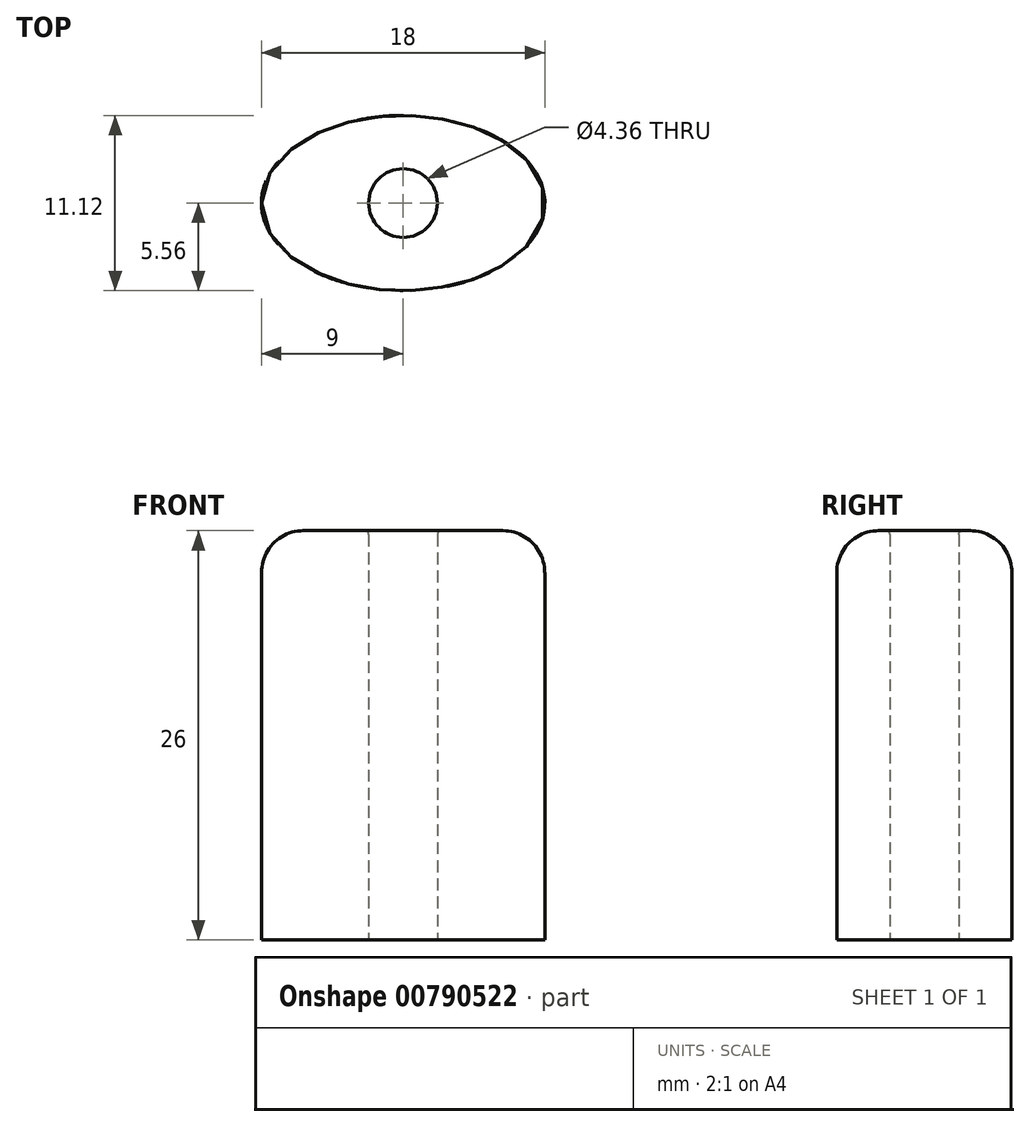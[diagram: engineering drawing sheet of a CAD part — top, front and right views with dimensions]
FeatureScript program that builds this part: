
annotation { "Feature Type Name" : "Feature", "Feature Type Description" : "" }
export const myFeature = defineFeature(function(context is Context, id is Id, definition is map)
    precondition{}
    {
        {
            var Q0;
            Q0=qCreatedBy(makeId("Top.planeOp"),FACE);
            var sketch = newSketch(context, id + "F0", { "sketchPlane" : qUnion([Q0])});
            skEllipse(sketch, "E0", {"center": v(0, 0) * mm, "majorRadius": 5.56 * mm, "minorRadius": 9 * mm, "majorAxis": v(0, 1)});
            skCircle(sketch, "E1", {"center": v(0, 0) * mm, "radius": 2.18 * mm});
            skSolve(sketch);
        }
        {
            var Q0;
            Q0=makeQuery(id+"F0.imprint","IMPRINT",FACE,{"disambiguationData":[TD([[makeQuery(id+"F0.imprint","IMPRINT",EDGE,{"derivedFrom":sQuery(id+"F0.wireOp",EDGE,"E0")}),1.0]])]});
            extrude(context, id + "F1", {"entities" : qUnion([Q0]), "depth" : 26 * mm, "offsetDistance" : 25 * mm});
        }
        {
            var Q0;
            Q0=makeQuery(id+"F1.opExtrude","CAP_EDGE",EDGE,{"disambiguationData":[OSD([sQuery(id+"F0.wireOp",EDGE,"E0")])],"isStart":false});
            fillet(context, id + "F2", {"entities" : qUnion([Q0]), "radius" : 2.66 * mm, "tangentPropagation" : true, "allowEdgeOverflow" : false});
        }
        {
            var Q0;
            Q0=makeQuery(id+"F1.opExtrude","CAP_EDGE",EDGE,{"disambiguationData":[OSD([sQuery(id+"F0.wireOp",EDGE,"E1")])],"isStart":false});
            fillet(context, id + "F3", {"entities" : qUnion([Q0]), "radius" : 0.24 * mm, "tangentPropagation" : true, "allowEdgeOverflow" : false});
        }
    });
